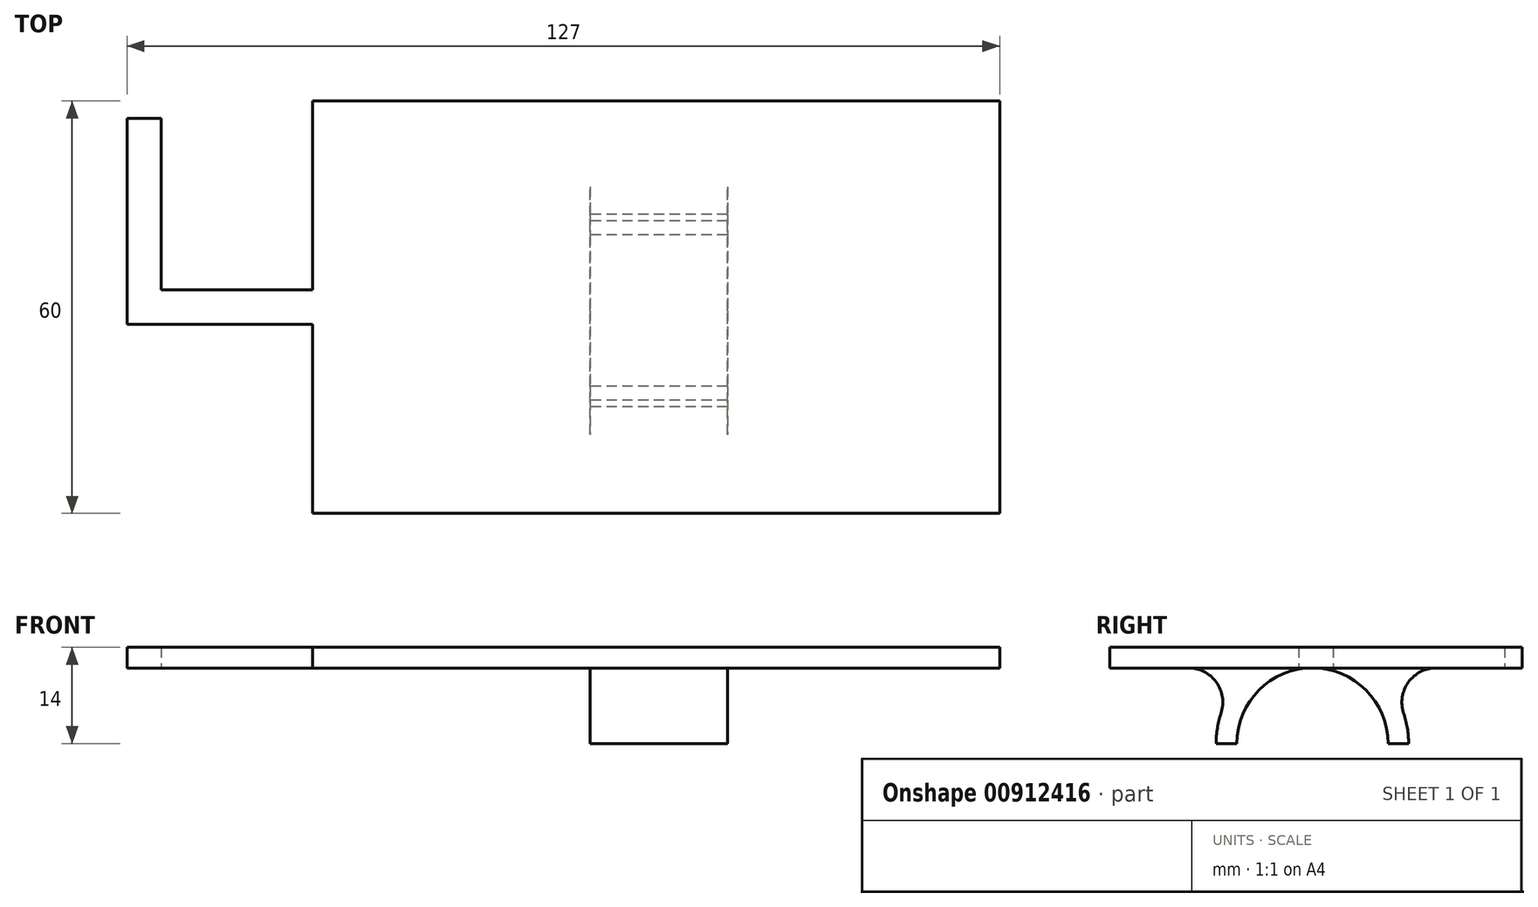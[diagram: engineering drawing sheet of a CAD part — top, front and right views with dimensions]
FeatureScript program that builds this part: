
annotation { "Feature Type Name" : "Feature", "Feature Type Description" : "" }
export const myFeature = defineFeature(function(context is Context, id is Id, definition is map)
    precondition{}
    {
        {
            var Q0;
            Q0=qCreatedBy(makeId("Top.planeOp"),FACE);
            var sketch = newSketch(context, id + "F0", { "sketchPlane" : qUnion([Q0])});
            skLineSegment(sketch, "E0.bottom", {"start": v(-50.38, 30.5) * mm, "end": v(49.62, 30.5) * mm});
            skLineSegment(sketch, "E0.top", {"start": v(-50.38, -29.5) * mm, "end": v(49.62, -29.5) * mm});
            skLineSegment(sketch, "E0.left", {"start": v(-50.38, 30.5) * mm, "end": v(-50.38, -29.5) * mm});
            skLineSegment(sketch, "E0.right", {"start": v(49.62, 30.5) * mm, "end": v(49.62, -29.5) * mm});
            skLineSegment(sketch, "E1.bottom", {"start": v(-50.38, -2) * mm, "end": v(-72.38, -2) * mm});
            skLineSegment(sketch, "E1.top", {"start": v(-50.38, 3) * mm, "end": v(-72.38, 3) * mm});
            skLineSegment(sketch, "E1.left", {"start": v(-50.38, -2) * mm, "end": v(-50.38, 3) * mm});
            skLineSegment(sketch, "E1.right", {"start": v(-72.38, -2) * mm, "end": v(-72.38, 3) * mm});
            skPoint(sketch, "E2", {"position": v(-50.38, 0.5) * mm});
            skLineSegment(sketch, "E3.bottom", {"start": v(-72.38, 28) * mm, "end": v(-77.38, 28) * mm});
            skLineSegment(sketch, "E3.top", {"start": v(-72.38, -2) * mm, "end": v(-77.38, -2) * mm});
            skLineSegment(sketch, "E3.left", {"start": v(-72.38, 28) * mm, "end": v(-72.38, -2) * mm});
            skLineSegment(sketch, "E3.right", {"start": v(-77.38, 28) * mm, "end": v(-77.38, -2) * mm});
            skSolve(sketch);
        }
        {
            var Q0;
            {var subQ3=sQuery(id+"F0.wireOp",EDGE,"E0.bottom");Q0=makeQuery(id+"F0.imprint","IMPRINT",FACE,{"disambiguationData":[TD([[makeQuery(id+"F0.imprint","IMPRINT",EDGE,{"derivedFrom":subQ3}),-1.0]])]});}
            var Q1;
            Q1=makeQuery(id+"F0.imprint","IMPRINT",FACE,{"disambiguationData":[TD([[makeQuery(id+"F0.imprint","IMPRINT",EDGE,{"derivedFrom":sQuery(id+"F0.wireOp",EDGE,"E1.bottom")}),-1.0]])]});
            var Q2;
            {var subQ3=sQuery(id+"F0.wireOp",EDGE,"E3.bottom");Q2=makeQuery(id+"F0.imprint","IMPRINT",FACE,{"disambiguationData":[TD([[makeQuery(id+"F0.imprint","IMPRINT",EDGE,{"derivedFrom":subQ3}),1.0]])]});}
            extrude(context, id + "F1", {"entities" : qUnion([Q0, Q1, Q2]), "depth" : 3 * mm, "offsetDistance" : 25 * mm});
        }
        {
            var Q0;
            Q0=qCreatedBy(makeId("Right.planeOp"),FACE);
            var sketch = newSketch(context, id + "F2", { "sketchPlane" : qUnion([Q0])});
            skCircle(sketch, "E4", {"center": v(0, -11) * mm, "radius": 11 * mm});
            skCircle(sketch, "E5", {"center": v(0, -11) * mm, "radius": 14 * mm});
            skLineSegment(sketch, "E6", {"start": v(14, -11) * mm, "end": v(-14, -11) * mm});
            skSolve(sketch);
        }
        {
            var Q0;
            {var subQ0=sQuery(id+"F2.wireOp",EDGE,"E6");var subQ1=sQuery(id+"F2.wireOp",EDGE,"E4");var subQ2=makeQuery(id+"F2.imprint","INTERSECT",VERTEX,{"disambiguationData":[OD(0.0)],"derivedFrom":[subQ1,subQ0]});Q0=makeQuery(id+"F2.imprint","IMPRINT",FACE,{"disambiguationData":[TD([[makeQuery(id+"F2.imprint","IMPRINT",EDGE,{"disambiguationData":[TD([[subQ2,-1.0]])],"derivedFrom":subQ1}),-1.0]])]});}
            extrude(context, id + "F3", {"entities" : qUnion([Q0]), "operationType" : NewBodyOperationType.ADD, "endBound" : BoundingType.SYMMETRIC, "depth" : 20 * mm, "offsetDistance" : 25 * mm});
        }
        {
            var Q0;
            Q0=makeQuery(id+"F3.boolean.opBoolean","INTERSECT",EDGE,{"disambiguationData":[OD(0.0)],"derivedFrom":[makeQuery(id+"F1.opExtrude","CAP_FACE",FACE,{"disambiguationData":[OSD([sQuery(id+"F0.wireOp",EDGE,"E0.bottom"),sQuery(id+"F0.wireOp",EDGE,"E0.top"),sQuery(id+"F0.wireOp",EDGE,"E0.left"),sQuery(id+"F0.wireOp",EDGE,"E0.right"),sQuery(id+"F0.wireOp",EDGE,"E1.bottom"),sQuery(id+"F0.wireOp",EDGE,"E1.top"),sQuery(id+"F0.wireOp",EDGE,"E1.right")])],"isStart":true}),makeQuery(id+"F3.opExtrude","SWEPT_FACE",FACE,{"disambiguationData":[OSD([sQuery(id+"F2.wireOp",EDGE,"E5")])]})]});
            var Q1;
            Q1=makeQuery(id+"F3.boolean.opBoolean","INTERSECT",EDGE,{"disambiguationData":[OD(1.0)],"derivedFrom":[makeQuery(id+"F1.opExtrude","CAP_FACE",FACE,{"disambiguationData":[OSD([sQuery(id+"F0.wireOp",EDGE,"E0.bottom"),sQuery(id+"F0.wireOp",EDGE,"E0.top"),sQuery(id+"F0.wireOp",EDGE,"E0.left"),sQuery(id+"F0.wireOp",EDGE,"E0.right"),sQuery(id+"F0.wireOp",EDGE,"E1.bottom"),sQuery(id+"F0.wireOp",EDGE,"E1.top"),sQuery(id+"F0.wireOp",EDGE,"E1.right")])],"isStart":true}),makeQuery(id+"F3.opExtrude","SWEPT_FACE",FACE,{"disambiguationData":[OSD([sQuery(id+"F2.wireOp",EDGE,"E5")])]})]});
            fillet(context, id + "F4", {"entities" : qUnion([Q0, Q1]), "radius" : 5 * mm, "tangentPropagation" : true, "allowEdgeOverflow" : false});
        }
    });
